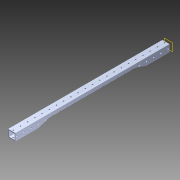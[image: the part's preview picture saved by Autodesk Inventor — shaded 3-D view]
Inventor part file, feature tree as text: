
AUTODESK INVENTOR PART (.ipt)
format: ipt  version: 2014 SP1 (Build 180222100, 222)  size: 1,305,600 bytes
history: native  units: in
note: dims shown in document units (in); Inventor stores cm internally (conversion verified against a paired STEP export)
features: extrude x3, sketch x3, pattern_circular x1, other x1, plane x1, imported_body x1, projected_geometry x1
ambient origin geometry x8: Origin, YZ Plane, XZ Plane, XY Plane, X Axis, Y Axis, Z Axis, Center Point
bodies: Body1 (feature_tree)
feature tree (11):
  pattern_circular  "CirPattern2"
  other  "217-3426-STEP1"
  plane  "Work Plane1"
  extrude  "Extrusion1"  Depth=3937.0079in TaperAngle=0.0deg
  extrude  "Extrusion2"  Depth=21.375in
  extrude  "Extrusion3"  Depth=1.0in TaperAngle=0.0deg
  imported_body  "Base1"
  sketch  "Sketch1"  dims[d0=-22.0in d1=3937.0079in d2=0.0in]
  sketch  "Sketch3"  dims[d3=21.375in d4=11.0in]
  projected_geometry  "Projected Loop1"
  sketch  "Sketch4"  dims[d5=2.0in d6=0.0in d7=1.0in d8=0.0in d9=1.5in d10=1.5in]
